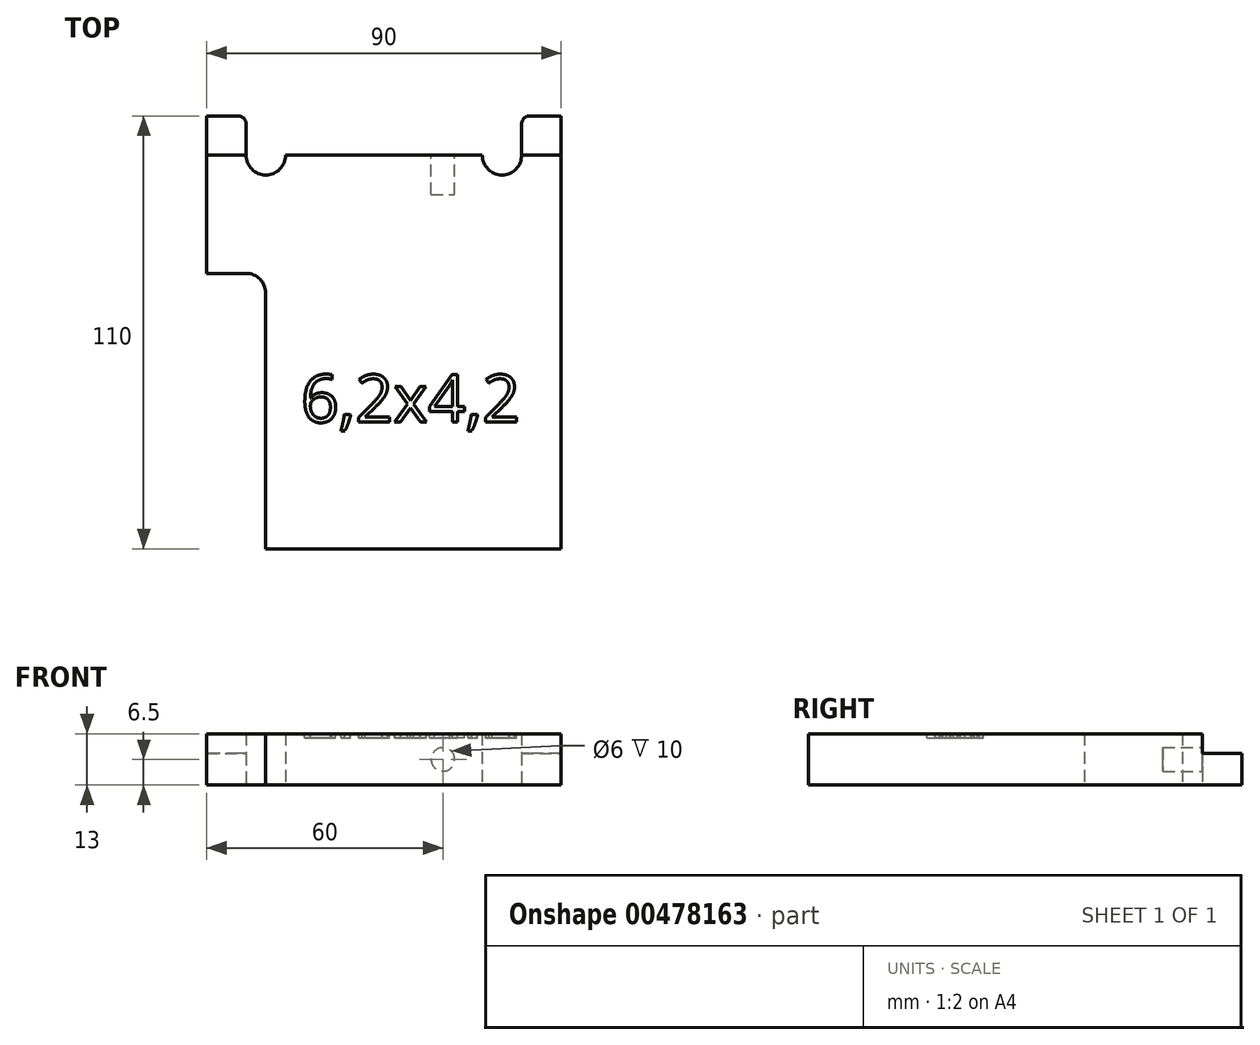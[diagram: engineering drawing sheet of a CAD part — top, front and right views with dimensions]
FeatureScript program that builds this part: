
annotation { "Feature Type Name" : "Feature", "Feature Type Description" : "" }
export const myFeature = defineFeature(function(context is Context, id is Id, definition is map)
    precondition{}
    {
        {
            var Q0;
            Q0=qCreatedBy(makeId("Top.planeOp"),FACE);
            var sketch = newSketch(context, id + "F0", { "sketchPlane" : qUnion([Q0])});
            skLineSegment(sketch, "E0", {"start": v(-42.48, -10.08) * mm, "end": v(-32.51, -10.08) * mm});
            skLineSegment(sketch, "E1", {"start": v(-27.51, -15.08) * mm, "end": v(-27.51, -80.08) * mm});
            skLineSegment(sketch, "E2", {"start": v(-27.51, -80.08) * mm, "end": v(47.52, -80.08) * mm});
            skLineSegment(sketch, "E3", {"start": v(47.52, -80.08) * mm, "end": v(47.52, 29.92) * mm});
            skLineSegment(sketch, "E4", {"start": v(47.52, 29.92) * mm, "end": v(39.52, 29.92) * mm});
            skLineSegment(sketch, "E5", {"start": v(37.52, 27.92) * mm, "end": v(37.52, 19.92) * mm});
            skLineSegment(sketch, "E6", {"start": v(-32.48, 19.92) * mm, "end": v(-32.48, 27.92) * mm});
            skLineSegment(sketch, "E7", {"start": v(-34.48, 29.92) * mm, "end": v(-42.48, 29.92) * mm});
            skLineSegment(sketch, "E8", {"start": v(-42.48, 29.92) * mm, "end": v(-42.48, -10.08) * mm});
            skPoint(sketch, "E9.visualSharp", {"position": v(-27.51, -10.08) * mm});
            skArc(sketch, "E9.filletArc", {"start": v(-27.51, -15.08) * mm, "mid": v(-28.97, -11.54) * mm, "end": v(-32.51, -10.08) * mm});
            skPoint(sketch, "E10.visualSharp", {"position": v(-32.48, 29.92) * mm});
            skArc(sketch, "E10.filletArc", {"start": v(-32.48, 27.92) * mm, "mid": v(-33.07, 29.33) * mm, "end": v(-34.48, 29.92) * mm});
            skPoint(sketch, "E11.visualSharp", {"position": v(37.52, 29.92) * mm});
            skArc(sketch, "E11.filletArc", {"start": v(39.52, 29.92) * mm, "mid": v(38.1, 29.33) * mm, "end": v(37.52, 27.92) * mm});
            skArc(sketch, "E12", {"start": v(-32.48, 19.92) * mm, "mid": v(-27.48, 14.92) * mm, "end": v(-22.48, 19.92) * mm});
            skArc(sketch, "E13", {"start": v(27.52, 19.92) * mm, "mid": v(32.52, 14.92) * mm, "end": v(37.52, 19.92) * mm});
            skLineSegment(sketch, "E14", {"start": v(-22.48, 19.92) * mm, "end": v(27.52, 19.92) * mm});
            skSolve(sketch);
        }
        {
            var Q0;
            Q0=makeQuery(id+"F0.imprint","IMPRINT",FACE,{"disambiguationData":[TD([[makeQuery(id+"F0.imprint","IMPRINT",EDGE,{"derivedFrom":sQuery(id+"F0.wireOp",EDGE,"E0")}),1.0]])]});
            extrude(context, id + "F1", {"entities" : qUnion([Q0]), "depth" : 13 * mm});
        }
        {
            var Q0;
            Q0=makeQuery(id+"F1.opExtrude","CAP_FACE",FACE,{"disambiguationData":[OSD([sQuery(id+"F0.wireOp",EDGE,"E0"),sQuery(id+"F0.wireOp",EDGE,"E1"),sQuery(id+"F0.wireOp",EDGE,"E2"),sQuery(id+"F0.wireOp",EDGE,"E3"),sQuery(id+"F0.wireOp",EDGE,"E4"),sQuery(id+"F0.wireOp",EDGE,"E5"),sQuery(id+"F0.wireOp",EDGE,"mmM2Y2U2-RtFC-ikFc-wxJO-fWfLtijxp1iX"),sQuery(id+"F0.wireOp",EDGE,"E6"),sQuery(id+"F0.wireOp",EDGE,"E7"),sQuery(id+"F0.wireOp",EDGE,"E8"),sQuery(id+"F0.wireOp",EDGE,"E9.filletArc"),sQuery(id+"F0.wireOp",EDGE,"E10.filletArc"),sQuery(id+"F0.wireOp",EDGE,"E11.filletArc")])],"isStart":false});
            var sketch = newSketch(context, id + "F2", { "sketchPlane" : qUnion([Q0])});
            skLineSegment(sketch, "E15.bottom", {"start": v(-43.08, 34.42) * mm, "end": v(64.23, 34.42) * mm});
            skLineSegment(sketch, "E15.top", {"start": v(-43.08, 19.92) * mm, "end": v(64.23, 19.92) * mm});
            skLineSegment(sketch, "E15.left", {"start": v(-43.08, 34.42) * mm, "end": v(-43.08, 19.92) * mm});
            skLineSegment(sketch, "E15.right", {"start": v(64.23, 34.42) * mm, "end": v(64.23, 19.92) * mm});
            skSolve(sketch);
        }
        {
            var Q0;
            Q0 = qSketchRegion(id + "F2", true);
            extrude(context, id + "F3", {"entities" : qUnion([Q0]), "operationType" : NewBodyOperationType.REMOVE, "oppositeDirection" : true, "depth" : 5 * mm});
        }
        {
            var Q0;
            Q0=makeQuery(id+"F1.opExtrude","SWEPT_FACE",FACE,{"disambiguationData":[OSD([sQuery(id+"F0.wireOp",EDGE,"E14")])]});
            var sketch = newSketch(context, id + "F4", { "sketchPlane" : qUnion([Q0])});
            skCircle(sketch, "E16", {"center": v(-17.52, 6.5) * mm, "radius": 3 * mm});
            skSolve(sketch);
        }
        {
            var Q0;
            Q0 = qSketchRegion(id + "F4", true);
            extrude(context, id + "F5", {"entities" : qUnion([Q0]), "operationType" : NewBodyOperationType.REMOVE, "oppositeDirection" : true, "depth" : 10 * mm});
        }
        {
            var Q0;
            Q0=makeQuery(id+"F1.opExtrude","CAP_FACE",FACE,{"disambiguationData":[OSD([sQuery(id+"F0.wireOp",EDGE,"E0"),sQuery(id+"F0.wireOp",EDGE,"E1"),sQuery(id+"F0.wireOp",EDGE,"E2"),sQuery(id+"F0.wireOp",EDGE,"E3"),sQuery(id+"F0.wireOp",EDGE,"E4"),sQuery(id+"F0.wireOp",EDGE,"E5"),sQuery(id+"F0.wireOp",EDGE,"E6"),sQuery(id+"F0.wireOp",EDGE,"E7"),sQuery(id+"F0.wireOp",EDGE,"E8"),sQuery(id+"F0.wireOp",EDGE,"E9.filletArc"),sQuery(id+"F0.wireOp",EDGE,"E10.filletArc"),sQuery(id+"F0.wireOp",EDGE,"E11.filletArc"),sQuery(id+"F0.wireOp",EDGE,"E12"),sQuery(id+"F0.wireOp",EDGE,"E13"),sQuery(id+"F0.wireOp",EDGE,"E14")])],"isStart":false});
            var sketch = newSketch(context, id + "F6", { "sketchPlane" : qUnion([Q0])});
            skText(sketch, "E17", { "text": "6,2x4,2", "fontName": "OpenSans-Regular.ttf"});
            const initialGuessF6  = {"E17": [-0.01854, -0.0479, 1, 0, 0.01214]};
            skSetInitialGuess(sketch, initialGuessF6);
            skSolve(sketch);
        }
        {
            var Q0;
            Q0 = qSketchRegion(id + "F6", true);
            extrude(context, id + "F7", {"entities" : qUnion([Q0]), "operationType" : NewBodyOperationType.REMOVE, "oppositeDirection" : true, "depth" : 1 * mm});
        }
    });
